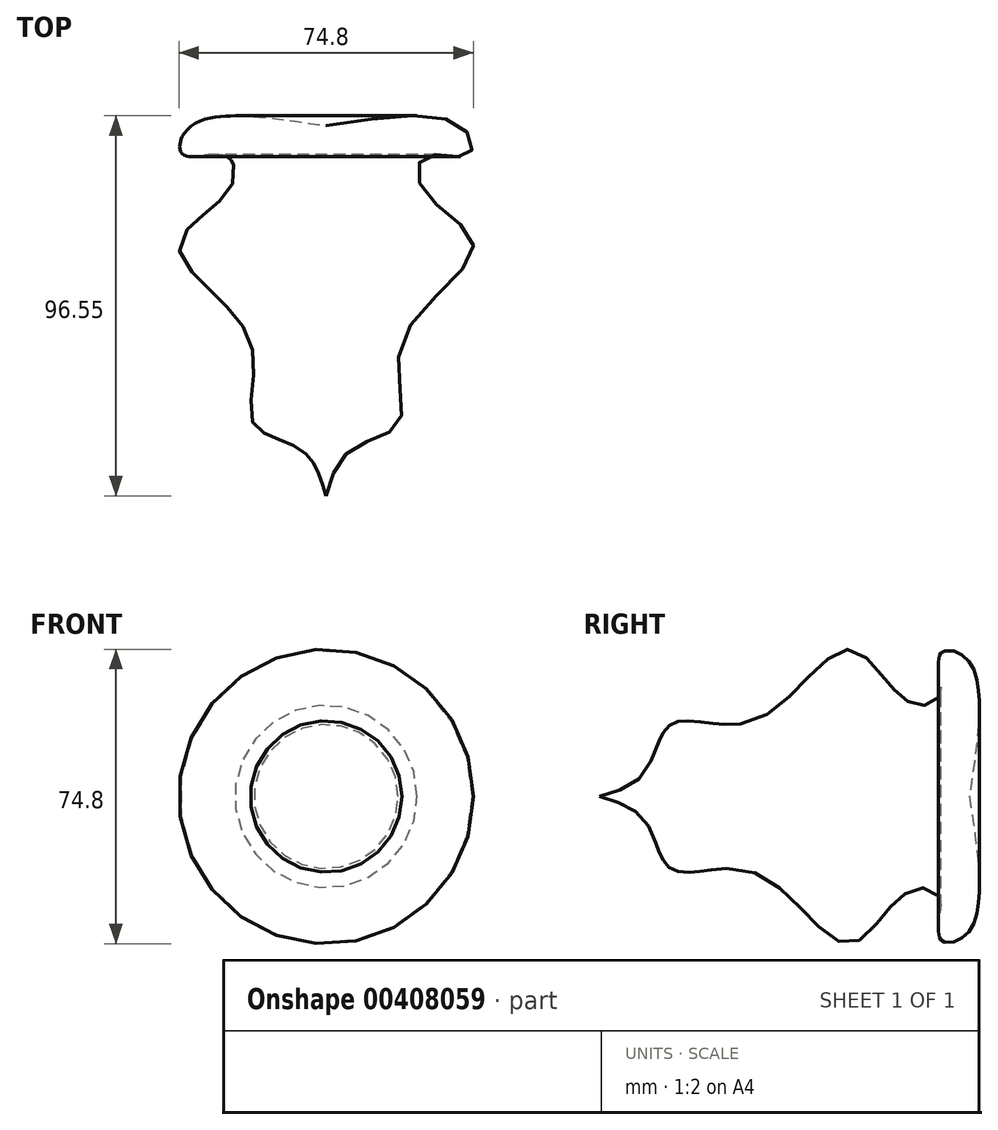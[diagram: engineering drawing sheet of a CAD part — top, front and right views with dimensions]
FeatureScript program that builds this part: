
annotation { "Feature Type Name" : "Feature", "Feature Type Description" : "" }
export const myFeature = defineFeature(function(context is Context, id is Id, definition is map)
    precondition{}
    {
        {
            var Q0;
            Q0=qCreatedBy(makeId("Top.planeOp"),FACE);
            var sketch = newSketch(context, id + "F0", { "sketchPlane" : qUnion([Q0])});
            skLineSegment(sketch, "E0", {"start": v(0, 77.17) * mm, "end": v(0, -75.23) * mm});
            skFitSpline(sketch, "E1", {"points": [v(0, 38.97) * mm, v(34.6, 38.68) * mm, v(36.28, 31.64) * mm, v(25.6, 31.36) * mm, v(24.47, 22.92) * mm, v(37.4, 8.28) * mm, v(19.41, -15.35) * mm, v(18.57, -36.46) * mm, v(6.48, -43.21) * mm, v(0, -55.03) * mm], "startDerivative": vector(269.97, 42.22) * mm, "endDerivative": vector(-40.11, -137.9) * mm});
            skSolve(sketch);
        }
        {
            var Q0;
            {var subQ0=sQuery(id+"F0.wireOp",EDGE,"E1");Q0=makeQuery(id+"F0.imprint","IMPRINT",FACE,{"disambiguationData":[TD([[makeQuery(id+"F0.imprint","IMPRINT",EDGE,{"derivedFrom":subQ0}),-1.0]])]});}
            var Q1;
            Q1=sQuery(id+"F0.wireOp",EDGE,"E0");
            revolve(context, id + "F1", {"entities" : qUnion([Q0]), "axis" : qUnion([Q1]), "revolveType" : RevolveType.FULL});
        }
    });
